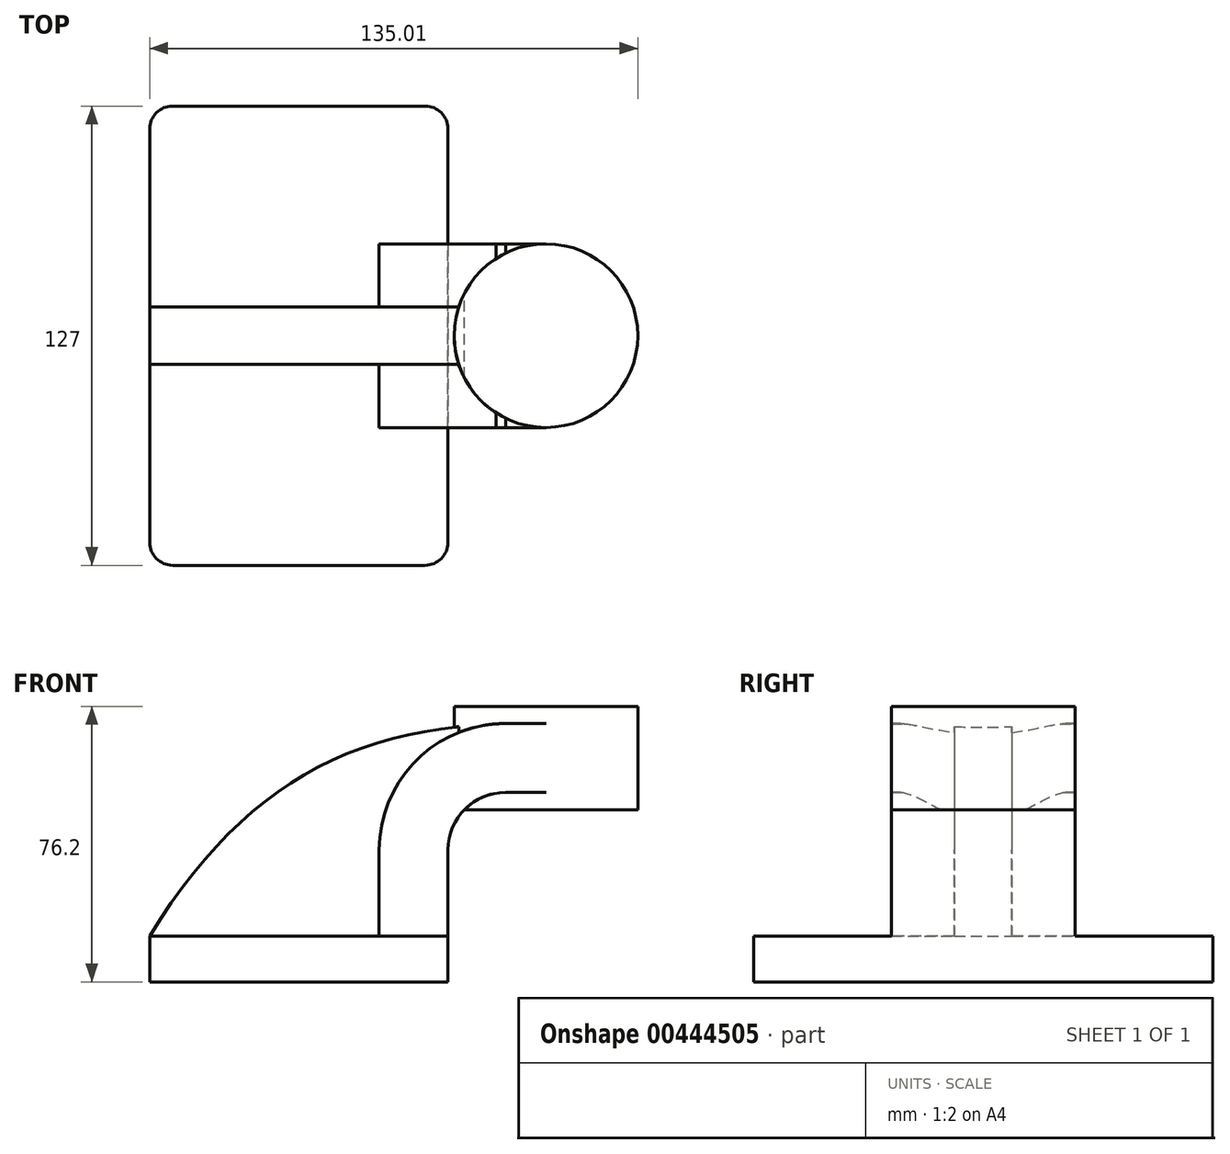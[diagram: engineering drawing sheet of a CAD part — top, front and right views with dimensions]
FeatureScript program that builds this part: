
annotation { "Feature Type Name" : "Feature", "Feature Type Description" : "" }
export const myFeature = defineFeature(function(context is Context, id is Id, definition is map)
    precondition{}
    {
        {
            var Q0;
            Q0=qCreatedBy(makeId("Front.planeOp"),FACE);
            var sketch = newSketch(context, id + "F0", { "sketchPlane" : qUnion([Q0])});
            skLineSegment(sketch, "E0.bottom", {"start": v(41.28, 6.35) * mm, "end": v(-41.28, 6.35) * mm});
            skLineSegment(sketch, "E0.top", {"start": v(41.28, -6.35) * mm, "end": v(-41.27, -6.35) * mm});
            skLineSegment(sketch, "E0.left", {"start": v(41.28, 6.35) * mm, "end": v(41.28, -6.35) * mm});
            skLineSegment(sketch, "E0.right", {"start": v(-41.28, 6.35) * mm, "end": v(-41.28, -6.35) * mm});
            skPoint(sketch, "E0.middle", {"position": v(0, 0) * mm});
            skLineSegment(sketch, "E1.bottom", {"start": v(119.13, 69.85) * mm, "end": v(68.33, 69.85) * mm});
            skLineSegment(sketch, "E1.top", {"start": v(119.13, 41.28) * mm, "end": v(68.33, 41.28) * mm});
            skLineSegment(sketch, "E1.left", {"start": v(119.13, 69.85) * mm, "end": v(119.13, 41.28) * mm});
            skLineSegment(sketch, "E1.right", {"start": v(68.33, 69.85) * mm, "end": v(68.33, 41.28) * mm});
            skPoint(sketch, "E1.middle", {"position": v(93.73, 55.56) * mm});
            skLineSegment(sketch, "E2", {"start": v(41.28, 6.35) * mm, "end": v(41.28, 30.18) * mm});
            skArc(sketch, "E3", {"start": v(41.28, 30.18) * mm, "mid": v(45.92, 41.4) * mm, "end": v(57.15, 46.05) * mm});
            skPoint(sketch, "E4.endSnap0", {"position": v(45.92, 41.4) * mm});
            skLineSegment(sketch, "E5", {"start": v(57.15, 46.05) * mm, "end": v(93.73, 46.05) * mm});
            skArc(sketch, "E6.0", {"start": v(22.23, 30.18) * mm, "mid": v(32.45, 54.87) * mm, "end": v(57.15, 65.1) * mm});
            skLineSegment(sketch, "E6.1", {"start": v(22.22, 6.35) * mm, "end": v(22.22, 30.18) * mm});
            skLineSegment(sketch, "E7.0", {"start": v(57.15, 65.1) * mm, "end": v(93.73, 65.1) * mm});
            skFitSpline(sketch, "E8", {"points": [v(57.15, 65.1) * mm, v(-41.28, 6.35) * mm], "startDerivative": vector(-133.02, -4.03) * mm, "endDerivative": vector(-75.24, -121.88) * mm});
            skLineSegment(sketch, "E9", {"start": v(93.73, 69.85) * mm, "end": v(93.73, 41.28) * mm});
            skSolve(sketch);
        }
        {
            var Q0;
            Q0=makeQuery(id+"F0.imprint","IMPRINT",FACE,{"disambiguationData":[TD([[makeQuery(id+"F0.imprint","IMPRINT",EDGE,{"derivedFrom":sQuery(id+"F0.wireOp",EDGE,"E0.top")}),-1.0]])]});
            extrude(context, id + "F1", {"entities" : qUnion([Q0]), "endBound" : BoundingType.SYMMETRIC, "oppositeDirection" : true, "depth" : 127 * mm});
        }
        {
            var Q0;
            {var subQ1=sQuery(id+"F0.wireOp",EDGE,"E2");Q0=makeQuery(id+"F0.imprint","IMPRINT",FACE,{"disambiguationData":[TD([[makeQuery(id+"F0.imprint","IMPRINT",EDGE,{"derivedFrom":subQ1}),1.0]])]});}
            extrude(context, id + "F2", {"entities" : qUnion([Q0]), "operationType" : NewBodyOperationType.ADD, "endBound" : BoundingType.SYMMETRIC, "depth" : 50.8 * mm});
        }
        {
            var Q0;
            {var subQ3=sQuery(id+"F0.wireOp",EDGE,"E6.1");Q0=makeQuery(id+"F0.imprint","IMPRINT",FACE,{"disambiguationData":[TD([[makeQuery(id+"F0.imprint","IMPRINT",EDGE,{"derivedFrom":subQ3}),1.0]])]});}
            extrude(context, id + "F3", {"entities" : qUnion([Q0]), "operationType" : NewBodyOperationType.ADD, "endBound" : BoundingType.SYMMETRIC, "depth" : 15.88 * mm});
        }
        {
            var Q0;
            {var subQ0=sQuery(id+"F0.wireOp",EDGE,"E7.0");var subQ1=sQuery(id+"F0.wireOp",EDGE,"E1.right");var subQ2=makeQuery(id+"F0.imprint","INTERSECT",VERTEX,{"derivedFrom":[subQ1,subQ0]});Q0=makeQuery(id+"F0.imprint","IMPRINT",FACE,{"disambiguationData":[TD([[makeQuery(id+"F0.imprint","IMPRINT",EDGE,{"disambiguationData":[TD([[subQ2,-1.0]])],"derivedFrom":subQ1}),1.0]])]});}
            var Q1;
            {var subQ0=sQuery(id+"F0.wireOp",EDGE,"E1.right");var subQ1=sQuery(id+"F0.wireOp",EDGE,"E1.top");var subQ2=makeQuery(id+"F0.imprint","INTERSECT",VERTEX,{"derivedFrom":[subQ1,subQ0]});Q1=makeQuery(id+"F0.imprint","IMPRINT",FACE,{"disambiguationData":[TD([[makeQuery(id+"F0.imprint","IMPRINT",EDGE,{"disambiguationData":[TD([[subQ2,1.0]])],"derivedFrom":subQ1}),-1.0]])]});}
            var Q2;
            {var subQ0=sQuery(id+"F0.wireOp",EDGE,"E1.right");var subQ1=sQuery(id+"F0.wireOp",EDGE,"E1.bottom");var subQ2=makeQuery(id+"F0.imprint","INTERSECT",VERTEX,{"derivedFrom":[subQ1,subQ0]});Q2=makeQuery(id+"F0.imprint","IMPRINT",FACE,{"disambiguationData":[TD([[makeQuery(id+"F0.imprint","IMPRINT",EDGE,{"disambiguationData":[TD([[subQ2,1.0]])],"derivedFrom":subQ1}),1.0]])]});}
            var Q3;
            Q3=sQuery(id+"F0.wireOp",EDGE,"E1.right");
            revolve(context, id + "F4", {"operationType" : NewBodyOperationType.ADD, "entities" : qUnion([Q0, Q1, Q2]), "axis" : qUnion([Q3]), "revolveType" : RevolveType.FULL});
        }
        {
            var Q0;
            Q0=makeQuery(id+"F1.opExtrude","CAP_EDGE",EDGE,{"disambiguationData":[OSD([sQuery(id+"F0.wireOp",EDGE,"E0.left")])],"isStart":true});
            var Q1;
            Q1=makeQuery(id+"F1.opExtrude","CAP_EDGE",EDGE,{"disambiguationData":[OSD([sQuery(id+"F0.wireOp",EDGE,"E0.left")])],"isStart":false});
            var Q2;
            Q2=makeQuery(id+"F1.opExtrude","CAP_EDGE",EDGE,{"disambiguationData":[OSD([sQuery(id+"F0.wireOp",EDGE,"E0.right")])],"isStart":true});
            var Q3;
            Q3=makeQuery(id+"F1.opExtrude","CAP_EDGE",EDGE,{"disambiguationData":[OSD([sQuery(id+"F0.wireOp",EDGE,"E0.right")])],"isStart":false});
            fillet(context, id + "F5", {"entities" : qUnion([Q0, Q1, Q2, Q3]), "radius" : 6.35 * mm, "tangentPropagation" : true, "allowEdgeOverflow" : false});
        }
    });
